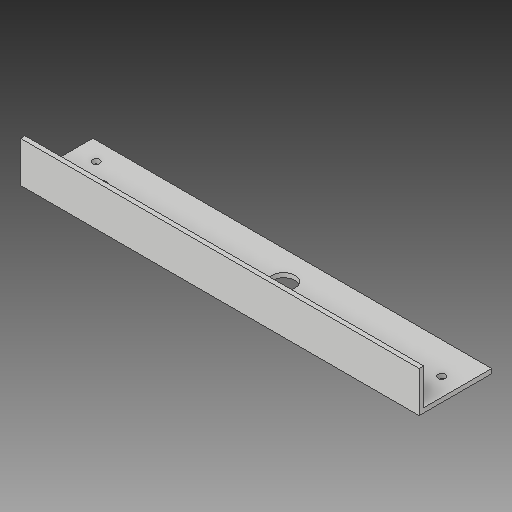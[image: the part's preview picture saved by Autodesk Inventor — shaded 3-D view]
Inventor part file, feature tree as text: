
AUTODESK INVENTOR PART (.ipt)
format: ipt  version: 2018 (Build 220112000, 112)  size: 105,984 bytes
history: native  units: in
note: dims shown in document units (in); Inventor stores cm internally (conversion verified against a paired STEP export)
features: sketch x4, other x3
ambient origin geometry x8: Origin, YZ Plane, XZ Plane, XY Plane, X Axis, Y Axis, Z Axis, Center Point
bodies: Solid1 (feature_tree)
feature tree (7):
  other  "angle iron with  holes 2_MIR.ipt"
  other  "Solid1::angle iron with  holes 2_MIR.ipt"
  other  "TaggingFeature1"
  sketch  "Sketch1"  dims[d0=0.3937in]
  sketch  "Sketch2"
  sketch  "Sketch3"
  sketch  "Sketch4"
